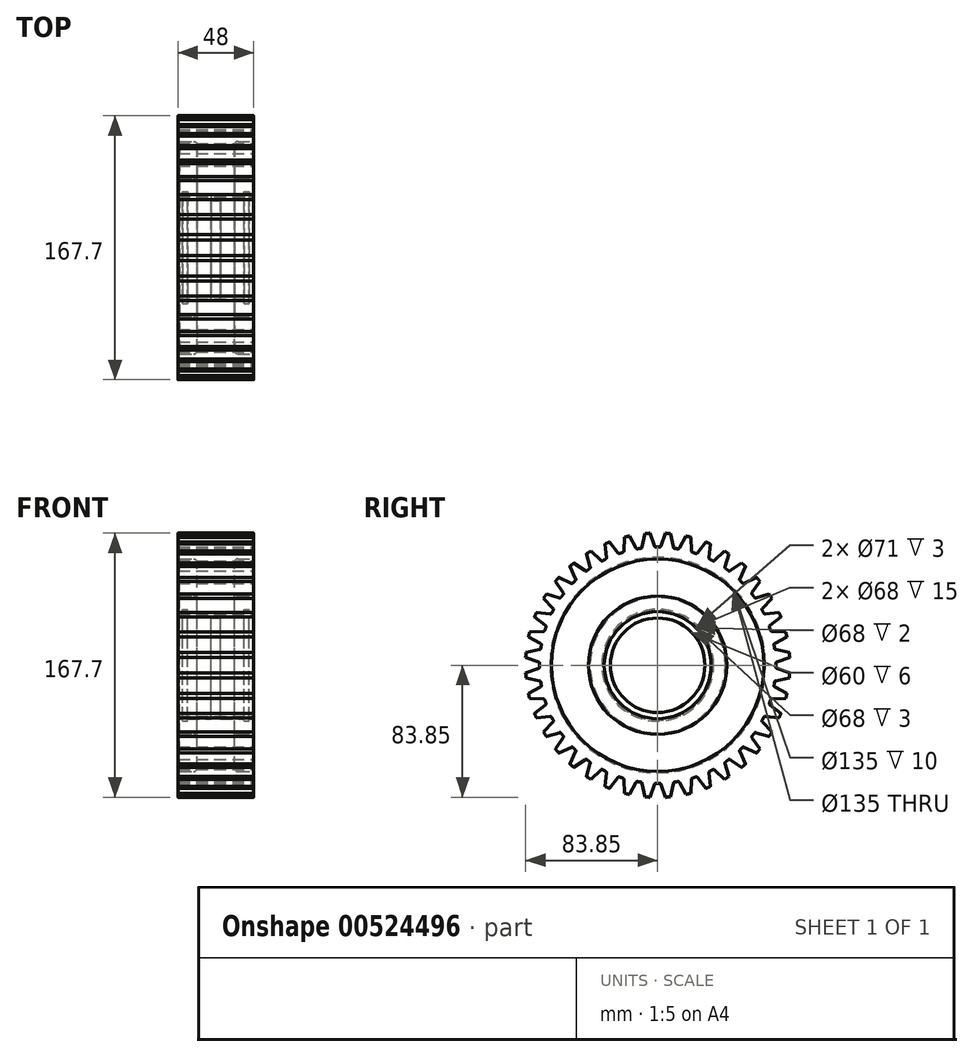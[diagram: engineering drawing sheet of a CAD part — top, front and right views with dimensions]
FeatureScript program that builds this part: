
annotation { "Feature Type Name" : "Feature", "Feature Type Description" : "" }
export const myFeature = defineFeature(function(context is Context, id is Id, definition is map)
    precondition{}
    {
        {
            var Q0;
            Q0=qCreatedBy(makeId("Front.planeOp"),FACE);
            var sketch = newSketch(context, id + "F0", { "sketchPlane" : qUnion([Q0])});
            skLineSegment(sketch, "E0.bottom", {"start": v(0, 0) * mm, "end": v(-24, 0) * mm, "construction": true});
            skLineSegment(sketch, "E0.top", {"start": v(0, 84) * mm, "end": v(-24, 84) * mm});
            skLineSegment(sketch, "E0.left", {"start": v(0, 0) * mm, "end": v(0, 84) * mm, "construction": true});
            skLineSegment(sketch, "E0.right", {"start": v(-24, 34) * mm, "end": v(-24, 44) * mm});
            skLineSegment(sketch, "E1", {"start": v(-24, 34) * mm, "end": v(-21, 34) * mm});
            skLineSegment(sketch, "E2", {"start": v(-21, 34) * mm, "end": v(-21, 35.5) * mm});
            skLineSegment(sketch, "E3", {"start": v(-21, 35.5) * mm, "end": v(-18, 35.5) * mm});
            skLineSegment(sketch, "E4", {"start": v(-18, 35.5) * mm, "end": v(-18, 34) * mm});
            skLineSegment(sketch, "E5", {"start": v(-18, 34) * mm, "end": v(-3, 34) * mm});
            skLineSegment(sketch, "E6", {"start": v(-3, 34) * mm, "end": v(-3, 30) * mm});
            skLineSegment(sketch, "E7", {"start": v(-3, 30) * mm, "end": v(0, 30) * mm});
            skLineSegment(sketch, "E8.bottom", {"start": v(-24, 44) * mm, "end": v(-14, 44) * mm});
            skLineSegment(sketch, "E8.top", {"start": v(-24, 67.5) * mm, "end": v(-14, 67.5) * mm});
            skLineSegment(sketch, "E8.right", {"start": v(-12, 65.5) * mm, "end": v(-12, 46) * mm});
            skLineSegment(sketch, "E9.trimOffspring", {"start": v(-24, 67.5) * mm, "end": v(-24, 84) * mm});
            skPoint(sketch, "E10.visualSharp", {"position": v(-12, 67.5) * mm});
            skArc(sketch, "E10.filletArc", {"start": v(-12, 65.5) * mm, "mid": v(-12.59, 66.91) * mm, "end": v(-14, 67.5) * mm});
            skPoint(sketch, "E11.visualSharp", {"position": v(-12, 44) * mm});
            skArc(sketch, "E11.filletArc", {"start": v(-14, 44) * mm, "mid": v(-12.59, 44.59) * mm, "end": v(-12, 46) * mm});
            skLineSegment(sketch, "E12.MirrorCS", {"start": v(0, 84) * mm, "end": v(24, 84) * mm});
            skLineSegment(sketch, "E13.MirrorCS", {"start": v(24, 67.5) * mm, "end": v(24, 84) * mm});
            skLineSegment(sketch, "E14.MirrorCS", {"start": v(24, 67.5) * mm, "end": v(14, 67.5) * mm});
            skArc(sketch, "E15.MirrorCS", {"start": v(12, 65.5) * mm, "mid": v(12.59, 66.91) * mm, "end": v(14, 67.5) * mm});
            skLineSegment(sketch, "E16.MirrorCS", {"start": v(12, 65.5) * mm, "end": v(12, 46) * mm});
            skArc(sketch, "E17.MirrorCS", {"start": v(14, 44) * mm, "mid": v(12.59, 44.59) * mm, "end": v(12, 46) * mm});
            skLineSegment(sketch, "E18.MirrorCS", {"start": v(24, 44) * mm, "end": v(14, 44) * mm});
            skLineSegment(sketch, "E19.MirrorCS", {"start": v(24, 34) * mm, "end": v(24, 44) * mm});
            skLineSegment(sketch, "E20.MirrorCS", {"start": v(24, 34) * mm, "end": v(21, 34) * mm});
            skLineSegment(sketch, "E21.MirrorCS", {"start": v(21, 35.5) * mm, "end": v(18, 35.5) * mm});
            skLineSegment(sketch, "E22.MirrorCS", {"start": v(18, 34) * mm, "end": v(3, 34) * mm});
            skLineSegment(sketch, "E23.MirrorCS", {"start": v(3, 34) * mm, "end": v(3, 30) * mm});
            skLineSegment(sketch, "E24.MirrorCS", {"start": v(3, 30) * mm, "end": v(0, 30) * mm});
            skLineSegment(sketch, "E25.MirrorCS", {"start": v(18, 35.5) * mm, "end": v(18, 34) * mm});
            skLineSegment(sketch, "E26.MirrorCS", {"start": v(21, 34) * mm, "end": v(21, 35.5) * mm});
            skSolve(sketch);
        }
        {
            var Q0;
            Q0=makeQuery(id+"F0.imprint","IMPRINT",FACE,{"disambiguationData":[TD([[makeQuery(id+"F0.imprint","IMPRINT",EDGE,{"derivedFrom":sQuery(id+"F0.wireOp",EDGE,"E0.top")}),1.0]])]});
            var Q1;
            Q1=sQuery(id+"F0.wireOp",EDGE,"E0.bottom");
            revolve(context, id + "F1", {"entities" : qUnion([Q0]), "axis" : qUnion([Q1]), "revolveType" : RevolveType.FULL});
        }
        {
            var Q0;
            Q0=qCreatedBy(makeId("Right.planeOp"),FACE);
            var sketch = newSketch(context, id + "F2", { "sketchPlane" : qUnion([Q0])});
            skArc(sketch, "E27", {"start": v(1.04, 75) * mm, "mid": v(0, 75) * mm, "end": v(-1.04, 75) * mm});
            skLineSegment(sketch, "E28", {"start": v(0, 0) * mm, "end": v(0, 84) * mm, "construction": true});
            skLineSegment(sketch, "E29", {"start": v(-2, 75.65) * mm, "end": v(-4.98, 83.85) * mm});
            skLineSegment(sketch, "E30.MirrorCS", {"start": v(2, 75.65) * mm, "end": v(4.98, 83.85) * mm});
            skPoint(sketch, "E31.visualSharp", {"position": v(1.75, 74.98) * mm});
            skArc(sketch, "E31.filletArc", {"start": v(1.04, 75) * mm, "mid": v(1.62, 75.17) * mm, "end": v(2, 75.65) * mm});
            skPoint(sketch, "E32.visualSharp", {"position": v(-1.75, 74.98) * mm});
            skArc(sketch, "E32.filletArc", {"start": v(-2, 75.65) * mm, "mid": v(-1.62, 75.17) * mm, "end": v(-1.04, 75) * mm});
            skArc(sketch, "E33", {"start": v(4.98, 83.85) * mm, "mid": v(0, 84) * mm, "end": v(-4.98, 83.85) * mm});
            skSolve(sketch);
        }
        {
            var Q0;
            Q0 = qSketchRegion(id + "F2", true);
            extrude(context, id + "F3", {"entities" : qUnion([Q0]), "operationType" : NewBodyOperationType.REMOVE, "endBound" : BoundingType.SYMMETRIC, "oppositeDirection" : true, "depth" : 48.8 * mm, "offsetDistance" : 25 * mm});
        }
        {
            var Q0;
            Q0=makeQuery(id+"F3.boolean.opBoolean","COPY",FACE,{"derivedFrom":makeQuery(id+"F3.opExtrude","SWEPT_FACE",FACE,{"disambiguationData":[OSD([sQuery(id+"F2.wireOp",EDGE,"E30.MirrorCS")])]})});
            var Q1;
            Q1=makeQuery(id+"F3.boolean.opBoolean","COPY",FACE,{"derivedFrom":makeQuery(id+"F3.opExtrude","SWEPT_FACE",FACE,{"disambiguationData":[OSD([sQuery(id+"F2.wireOp",EDGE,"E31.filletArc")])]})});
            var Q2;
            Q2=makeQuery(id+"F3.boolean.opBoolean","COPY",FACE,{"derivedFrom":makeQuery(id+"F3.opExtrude","SWEPT_FACE",FACE,{"disambiguationData":[OSD([sQuery(id+"F2.wireOp",EDGE,"E27")])]})});
            var Q3;
            Q3=makeQuery(id+"F3.boolean.opBoolean","COPY",FACE,{"derivedFrom":makeQuery(id+"F3.opExtrude","SWEPT_FACE",FACE,{"disambiguationData":[OSD([sQuery(id+"F2.wireOp",EDGE,"E32.filletArc")])]})});
            var Q4;
            Q4=makeQuery(id+"F3.boolean.opBoolean","COPY",FACE,{"derivedFrom":makeQuery(id+"F3.opExtrude","SWEPT_FACE",FACE,{"disambiguationData":[OSD([sQuery(id+"F2.wireOp",EDGE,"E29")])]})});
            var Q5;
            Q5=makeQuery(id+"F1.opRevolve","SWEPT_FACE",FACE,{"disambiguationData":[OSD([sQuery(id+"F0.wireOp",EDGE,"E0.top"),sQuery(id+"F0.wireOp",EDGE,"E12.MirrorCS")])]});
            circularPattern(context, id + "F4", {"patternType" : PatternType.FACE, "operationType" : NewBodyOperationType.REMOVE, "faces" : qUnion([Q0, Q1, Q2, Q3, Q4]), "axis" : qUnion([Q5]), "angle" : 360 * degree, "instanceCount" : 40, "equalSpace" : true});
        }
        {
            var Q0;
            Q0=makeQuery(id+"F1.opRevolve","SWEPT_EDGE",EDGE,{"disambiguationData":[OSD([sQuery(id+"F0.wireOp",EDGE,"E8.top"),sQuery(id+"F0.wireOp",EDGE,"E9.trimOffspring")])]});
            var Q1;
            Q1=makeQuery(id+"F1.opRevolve","SWEPT_EDGE",EDGE,{"disambiguationData":[OSD([sQuery(id+"F0.wireOp",EDGE,"E0.right"),sQuery(id+"F0.wireOp",EDGE,"E8.bottom")])]});
            var Q2;
            Q2=makeQuery(id+"F1.opRevolve","SWEPT_EDGE",EDGE,{"disambiguationData":[OSD([sQuery(id+"F0.wireOp",EDGE,"E0.right"),sQuery(id+"F0.wireOp",EDGE,"E1")])]});
            var Q3;
            Q3=makeQuery(id+"F1.opRevolve","SWEPT_EDGE",EDGE,{"disambiguationData":[OSD([sQuery(id+"F0.wireOp",EDGE,"E8.bottom"),sQuery(id+"F0.wireOp",EDGE,"E11.filletArc")])]});
            chamfer(context, id + "F5", {"entities" : qUnion([Q0, Q1, Q2, Q3]), "width" : 1 * mm, "tangentPropagation" : true});
        }
    });
